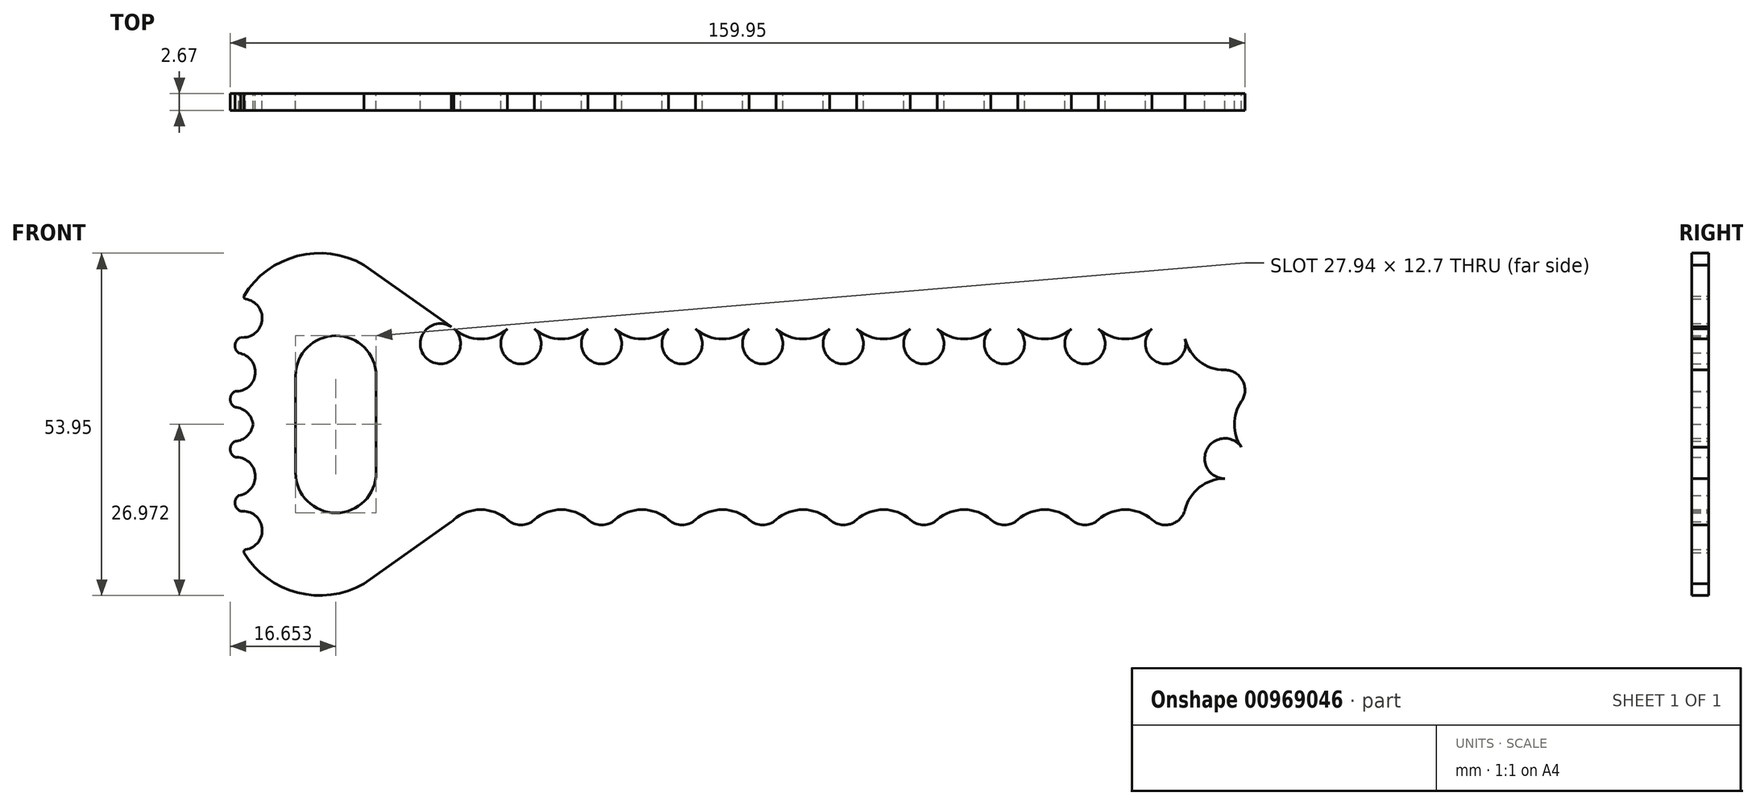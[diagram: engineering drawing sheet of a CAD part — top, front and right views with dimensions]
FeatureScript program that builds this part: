
annotation { "Feature Type Name" : "Feature", "Feature Type Description" : "" }
export const myFeature = defineFeature(function(context is Context, id is Id, definition is map)
    precondition{}
    {
        {
            var Q0;
            Q0=qCreatedBy(makeId("Front.planeOp"),FACE);
            var sketch = newSketch(context, id + "F0", { "sketchPlane" : qUnion([Q0])});
            skLineSegment(sketch, "E0.right", {"start": v(61.78, -7.38) * mm, "end": v(61.78, -7.89) * mm, "construction": true});
            skCircle(sketch, "E1.MirrorC", {"center": v(-65.29, -1.2) * mm, "radius": 3.18 * mm});
            skCircle(sketch, "E2", {"center": v(58.36, -8.5) * mm, "radius": 3.18 * mm});
            skArc(sketch, "E3.MirrorCS", {"start": v(-54.7, 1.16) * mm, "mid": v(-58.94, -0.46) * mm, "end": v(-63.17, 1.16) * mm});
            skCircle(sketch, "E4.MirrorC", {"center": v(-52.59, -1.2) * mm, "radius": 3.18 * mm});
            skCircle(sketch, "E5.MirrorC", {"center": v(-39.89, -1.2) * mm, "radius": 3.18 * mm});
            skCircle(sketch, "E6.MirrorC", {"center": v(-27.19, -1.2) * mm, "radius": 3.18 * mm});
            skCircle(sketch, "E7.MirrorC", {"center": v(-14.49, -1.2) * mm, "radius": 3.18 * mm});
            skCircle(sketch, "E8.MirrorC", {"center": v(-1.79, -1.2) * mm, "radius": 3.18 * mm});
            skCircle(sketch, "E9.MirrorC", {"center": v(10.91, -1.2) * mm, "radius": 3.18 * mm});
            skCircle(sketch, "E10.MirrorC", {"center": v(23.61, -1.2) * mm, "radius": 3.18 * mm});
            skCircle(sketch, "E11.MirrorC", {"center": v(36.31, -1.2) * mm, "radius": 3.18 * mm});
            skCircle(sketch, "E12.MirrorC", {"center": v(49.01, -1.2) * mm, "radius": 3.18 * mm});
            skArc(sketch, "E13.MirrorCS", {"start": v(-42, 1.16) * mm, "mid": v(-46.24, -0.46) * mm, "end": v(-50.47, 1.16) * mm});
            skArc(sketch, "E14.MirrorCS", {"start": v(-29.3, 1.16) * mm, "mid": v(-33.54, -0.46) * mm, "end": v(-37.77, 1.16) * mm});
            skArc(sketch, "E15.MirrorCS", {"start": v(-16.6, 1.16) * mm, "mid": v(-20.84, -0.46) * mm, "end": v(-25.07, 1.16) * mm});
            skArc(sketch, "E16.MirrorCS", {"start": v(-3.9, 1.16) * mm, "mid": v(-8.14, -0.46) * mm, "end": v(-12.37, 1.16) * mm});
            skArc(sketch, "E17.MirrorCS", {"start": v(8.8, 1.16) * mm, "mid": v(4.56, -0.46) * mm, "end": v(0.33, 1.16) * mm});
            skArc(sketch, "E18.MirrorCS", {"start": v(21.5, 1.16) * mm, "mid": v(17.26, -0.46) * mm, "end": v(13.03, 1.16) * mm});
            skArc(sketch, "E19.MirrorCS", {"start": v(34.2, 1.16) * mm, "mid": v(29.96, -0.46) * mm, "end": v(25.73, 1.16) * mm});
            skArc(sketch, "E20.MirrorCS", {"start": v(46.9, 1.16) * mm, "mid": v(42.66, -0.46) * mm, "end": v(38.43, 1.16) * mm});
            skArc(sketch, "E21", {"start": v(52.1, -0.47) * mm, "mid": v(54.36, -3.99) * mm, "end": v(58.33, -5.33) * mm});
            skArc(sketch, "E22", {"start": v(60.97, -10.3) * mm, "mid": v(60.14, -12.02) * mm, "end": v(59.86, -13.9) * mm});
            skPoint(sketch, "E23.middle", {"position": v(-75.42, -13.9) * mm});
            skArc(sketch, "E24", {"start": v(-62.11, -13.9) * mm, "mid": v(-65.29, -10.73) * mm, "end": v(-68.46, -13.9) * mm, "construction": true});
            skPoint(sketch, "E25.center", {"position": v(0.47, -13.9) * mm});
            skPoint(sketch, "E26.visualSharp", {"position": v(-88.5, 10.24) * mm});
            skArc(sketch, "E27.MirrorCS", {"start": v(-42, -3.57) * mm, "mid": v(-46.24, -1.96) * mm, "end": v(-50.47, -3.57) * mm, "construction": true});
            skArc(sketch, "E28.MirrorCS", {"start": v(-29.3, -3.57) * mm, "mid": v(-33.54, -1.96) * mm, "end": v(-37.77, -3.57) * mm, "construction": true});
            skArc(sketch, "E29.MirrorCS", {"start": v(-16.6, -3.57) * mm, "mid": v(-20.84, -1.96) * mm, "end": v(-25.07, -3.57) * mm, "construction": true});
            skArc(sketch, "E30.MirrorCS", {"start": v(-3.9, -3.57) * mm, "mid": v(-8.14, -1.96) * mm, "end": v(-12.37, -3.57) * mm, "construction": true});
            skArc(sketch, "E31.MirrorCS", {"start": v(8.8, -3.57) * mm, "mid": v(4.56, -1.96) * mm, "end": v(0.33, -3.57) * mm, "construction": true});
            skArc(sketch, "E32.MirrorCS", {"start": v(21.5, -3.57) * mm, "mid": v(17.26, -1.96) * mm, "end": v(13.03, -3.57) * mm, "construction": true});
            skArc(sketch, "E33.MirrorCS", {"start": v(34.2, -3.57) * mm, "mid": v(29.96, -1.96) * mm, "end": v(25.73, -3.57) * mm, "construction": true});
            skArc(sketch, "E34.MirrorCS", {"start": v(46.9, -3.57) * mm, "mid": v(42.66, -1.96) * mm, "end": v(38.43, -3.57) * mm, "construction": true});
            skArc(sketch, "E35", {"start": v(55.27, -9.25) * mm, "mid": v(53, -5.73) * mm, "end": v(49.04, -4.38) * mm, "construction": true});
            skArc(sketch, "E36", {"start": v(56.86, -13.9) * mm, "mid": v(56.58, -12.02) * mm, "end": v(55.74, -10.3) * mm, "construction": true});
            skCircle(sketch, "E37", {"center": v(-65.29, -1.2) * mm, "radius": 0.8 * mm, "construction": true});
            skArc(sketch, "E38", {"start": v(-64.49, -13.9) * mm, "mid": v(-65.29, -13.1) * mm, "end": v(-66.09, -13.9) * mm, "construction": true});
            skCircle(sketch, "E39", {"center": v(-52.59, -1.2) * mm, "radius": 0.8 * mm, "construction": true});
            skCircle(sketch, "E40", {"center": v(-39.89, -1.2) * mm, "radius": 0.8 * mm, "construction": true});
            skCircle(sketch, "E41", {"center": v(-27.19, -1.2) * mm, "radius": 0.8 * mm, "construction": true});
            skCircle(sketch, "E42", {"center": v(-14.49, -1.2) * mm, "radius": 0.8 * mm, "construction": true});
            skCircle(sketch, "E43", {"center": v(-1.79, -1.2) * mm, "radius": 0.8 * mm, "construction": true});
            skCircle(sketch, "E44", {"center": v(10.91, -1.2) * mm, "radius": 0.8 * mm, "construction": true});
            skCircle(sketch, "E45", {"center": v(23.61, -1.2) * mm, "radius": 0.8 * mm, "construction": true});
            skCircle(sketch, "E46", {"center": v(36.31, -1.2) * mm, "radius": 0.8 * mm, "construction": true});
            skCircle(sketch, "E47", {"center": v(49.01, -1.2) * mm, "radius": 0.8 * mm, "construction": true});
            skCircle(sketch, "E48", {"center": v(58.36, -8.5) * mm, "radius": 0.8 * mm, "construction": true});
            skArc(sketch, "E49", {"start": v(-54.7, -3.57) * mm, "mid": v(-58.94, -1.96) * mm, "end": v(-63.17, -3.57) * mm, "construction": true});
            skArc(sketch, "E50", {"start": v(-68.3, -12.92) * mm, "mid": v(-67.45, -7.56) * mm, "end": v(-68.3, -2.2) * mm, "construction": true});
            skArc(sketch, "E51", {"start": v(-63.4, -3.76) * mm, "mid": v(-63.9, -8.12) * mm, "end": v(-62.55, -12.3) * mm, "construction": true});
            skPoint(sketch, "E52.visualSharp", {"position": v(-96, 7.56) * mm});
            skArc(sketch, "E53", {"start": v(-96.74, -0.2) * mm, "mid": v(-93.4, 2.44) * mm, "end": v(-95.98, 5.82) * mm});
            skArc(sketch, "E54.2.0", {"start": v(48.77, 84.47) * mm, "mid": v(48.66, 79.8) * mm, "end": v(53.28, 80.57) * mm});
            skPoint(sketch, "E54.center", {"position": v(0, 0) * mm});
            skArc(sketch, "E55.1.0", {"start": v(-97.65, -8.72) * mm, "mid": v(-94.48, -5.99) * mm, "end": v(-97.06, -2.68) * mm});
            skArc(sketch, "E55.2.0", {"start": v(-94.83, -13.9) * mm, "mid": v(-95.76, -12.06) * mm, "end": v(-97.65, -11.23) * mm});
            skArc(sketch, "E56", {"start": v(-96.74, -0.2) * mm, "mid": v(-97.65, -1.34) * mm, "end": v(-97.06, -2.68) * mm});
            skArc(sketch, "E57", {"start": v(-97.65, -8.72) * mm, "mid": v(-98.42, -9.97) * mm, "end": v(-97.65, -11.23) * mm});
            skPoint(sketch, "E57.startSnap0", {"position": v(-97.65, -1.33) * mm});
            skPoint(sketch, "E57.endSnap0", {"position": v(-97.65, -1.33) * mm});
            skPoint(sketch, "E58.orphan", {"position": v(-97.77, -2.66) * mm});
            skArc(sketch, "E59", {"start": v(-96.27, 6.3) * mm, "mid": v(-96.23, 6) * mm, "end": v(-95.98, 5.82) * mm});
            skPoint(sketch, "E60.orphan", {"position": v(-96.41, 5.86) * mm});
            skPoint(sketch, "E61.orphan", {"position": v(-98.38, -8.6) * mm});
            skPoint(sketch, "E62.orphan", {"position": v(-98.37, -11.27) * mm});
            skArc(sketch, "E63.MirrorCS", {"start": v(-96.27, -34.12) * mm, "mid": v(-96.23, -33.82) * mm, "end": v(-95.98, -33.64) * mm});
            skCircle(sketch, "E64.MirrorC", {"center": v(-52.59, -26.6) * mm, "radius": 0.8 * mm, "construction": true});
            skCircle(sketch, "E65.MirrorC", {"center": v(-14.49, -26.6) * mm, "radius": 0.8 * mm, "construction": true});
            skCircle(sketch, "E66.MirrorC", {"center": v(23.61, -26.6) * mm, "radius": 0.8 * mm, "construction": true});
            skArc(sketch, "E67.MirrorCS", {"start": v(-96.74, -27.62) * mm, "mid": v(-97.65, -26.47) * mm, "end": v(-97.06, -25.13) * mm});
            skCircle(sketch, "E68.MirrorC", {"center": v(-65.29, -26.6) * mm, "radius": 0.8 * mm, "construction": true});
            skCircle(sketch, "E69.MirrorC", {"center": v(-27.19, -26.6) * mm, "radius": 0.8 * mm, "construction": true});
            skCircle(sketch, "E70.MirrorC", {"center": v(36.31, -26.6) * mm, "radius": 0.8 * mm, "construction": true});
            skCircle(sketch, "E71.MirrorC", {"center": v(-1.79, -26.6) * mm, "radius": 0.8 * mm, "construction": true});
            skCircle(sketch, "E72.MirrorC", {"center": v(10.91, -26.6) * mm, "radius": 0.8 * mm, "construction": true});
            skCircle(sketch, "E73.MirrorC", {"center": v(49.01, -26.6) * mm, "radius": 0.8 * mm, "construction": true});
            skCircle(sketch, "E74.MirrorC", {"center": v(-39.89, -26.6) * mm, "radius": 0.8 * mm, "construction": true});
            skPoint(sketch, "E75.MirrorP", {"position": v(-97.65, -26.48) * mm});
            skCircle(sketch, "E76.MirrorC", {"center": v(-27.19, -26.6) * mm, "radius": 3.18 * mm});
            skCircle(sketch, "E77.MirrorC", {"center": v(-65.29, -26.6) * mm, "radius": 3.18 * mm});
            skCircle(sketch, "E78.MirrorC", {"center": v(-52.59, -26.6) * mm, "radius": 3.18 * mm});
            skArc(sketch, "E79.MirrorCS", {"start": v(34.2, -28.97) * mm, "mid": v(29.96, -27.36) * mm, "end": v(25.73, -28.97) * mm});
            skArc(sketch, "E80.MirrorCS", {"start": v(21.5, -28.97) * mm, "mid": v(17.26, -27.36) * mm, "end": v(13.03, -28.97) * mm});
            skArc(sketch, "E81.MirrorCS", {"start": v(46.9, -24.24) * mm, "mid": v(42.66, -25.86) * mm, "end": v(38.43, -24.24) * mm, "construction": true});
            skArc(sketch, "E82.MirrorCS", {"start": v(46.9, -28.97) * mm, "mid": v(42.66, -27.36) * mm, "end": v(38.43, -28.97) * mm});
            skPoint(sketch, "E83.MirrorP", {"position": v(-97.77, -25.15) * mm});
            skArc(sketch, "E84.MirrorCS", {"start": v(-54.7, -28.97) * mm, "mid": v(-58.94, -27.36) * mm, "end": v(-63.17, -28.97) * mm});
            skCircle(sketch, "E85.MirrorC", {"center": v(-14.49, -26.6) * mm, "radius": 3.18 * mm});
            skArc(sketch, "E86.MirrorCS", {"start": v(34.2, -24.24) * mm, "mid": v(29.96, -25.86) * mm, "end": v(25.73, -24.24) * mm, "construction": true});
            skPoint(sketch, "E87.MirrorP", {"position": v(0, -27.82) * mm});
            skArc(sketch, "E88.MirrorCS", {"start": v(8.8, -28.97) * mm, "mid": v(4.56, -27.36) * mm, "end": v(0.33, -28.97) * mm});
            skArc(sketch, "E89.MirrorCS", {"start": v(-63.4, -24.06) * mm, "mid": v(-63.9, -19.7) * mm, "end": v(-62.55, -15.5) * mm, "construction": true});
            skArc(sketch, "E90.MirrorCS", {"start": v(-97.65, -19.1) * mm, "mid": v(-94.48, -21.83) * mm, "end": v(-97.06, -25.13) * mm});
            skArc(sketch, "E91.MirrorCS", {"start": v(-96.74, -27.62) * mm, "mid": v(-93.4, -30.26) * mm, "end": v(-95.98, -33.64) * mm});
            skCircle(sketch, "E92.MirrorC", {"center": v(23.61, -26.6) * mm, "radius": 3.18 * mm});
            skArc(sketch, "E93.MirrorCS", {"start": v(-42, -24.24) * mm, "mid": v(-46.24, -25.86) * mm, "end": v(-50.47, -24.24) * mm, "construction": true});
            skArc(sketch, "E94.MirrorCS", {"start": v(-42, -28.97) * mm, "mid": v(-46.24, -27.36) * mm, "end": v(-50.47, -28.97) * mm});
            skPoint(sketch, "E95.MirrorP", {"position": v(-96.41, -33.67) * mm});
            skCircle(sketch, "E96.MirrorC", {"center": v(36.31, -26.6) * mm, "radius": 3.18 * mm});
            skArc(sketch, "E97.MirrorCS", {"start": v(-3.9, -24.24) * mm, "mid": v(-8.14, -25.86) * mm, "end": v(-12.37, -24.24) * mm, "construction": true});
            skCircle(sketch, "E98.MirrorC", {"center": v(10.91, -26.6) * mm, "radius": 3.18 * mm});
            skArc(sketch, "E99.MirrorCS", {"start": v(21.5, -24.24) * mm, "mid": v(17.26, -25.86) * mm, "end": v(13.03, -24.24) * mm, "construction": true});
            skArc(sketch, "E100.MirrorCS", {"start": v(-68.3, -14.9) * mm, "mid": v(-67.45, -20.26) * mm, "end": v(-68.3, -25.62) * mm, "construction": true});
            skArc(sketch, "E101.MirrorCS", {"start": v(8.8, -24.24) * mm, "mid": v(4.56, -25.86) * mm, "end": v(0.33, -24.24) * mm, "construction": true});
            skArc(sketch, "E102.MirrorCS", {"start": v(55.27, -18.57) * mm, "mid": v(53, -22.09) * mm, "end": v(49.04, -23.43) * mm, "construction": true});
            skCircle(sketch, "E103.MirrorC", {"center": v(-1.79, -26.6) * mm, "radius": 3.18 * mm});
            skArc(sketch, "E104.MirrorCS", {"start": v(-16.6, -24.24) * mm, "mid": v(-20.84, -25.86) * mm, "end": v(-25.07, -24.24) * mm, "construction": true});
            skArc(sketch, "E105.MirrorCS", {"start": v(-54.7, -24.24) * mm, "mid": v(-58.94, -25.86) * mm, "end": v(-63.17, -24.24) * mm, "construction": true});
            skCircle(sketch, "E106.MirrorC", {"center": v(49.01, -26.6) * mm, "radius": 3.18 * mm});
            skArc(sketch, "E107.MirrorCS", {"start": v(-29.3, -28.97) * mm, "mid": v(-33.54, -27.36) * mm, "end": v(-37.77, -28.97) * mm});
            skArc(sketch, "E108.MirrorCS", {"start": v(-16.6, -28.97) * mm, "mid": v(-20.84, -27.36) * mm, "end": v(-25.07, -28.97) * mm});
            skCircle(sketch, "E109.MirrorC", {"center": v(58.36, -19.3) * mm, "radius": 3.18 * mm});
            skArc(sketch, "E110.MirrorCS", {"start": v(52.1, -27.35) * mm, "mid": v(54.36, -23.83) * mm, "end": v(58.33, -22.48) * mm});
            skArc(sketch, "E111.MirrorCS", {"start": v(-29.3, -24.24) * mm, "mid": v(-33.54, -25.86) * mm, "end": v(-37.77, -24.24) * mm, "construction": true});
            skCircle(sketch, "E112.MirrorC", {"center": v(-39.89, -26.6) * mm, "radius": 3.18 * mm});
            skArc(sketch, "E113.MirrorCS", {"start": v(-3.9, -28.97) * mm, "mid": v(-8.14, -27.36) * mm, "end": v(-12.37, -28.97) * mm});
            skArc(sketch, "E114.MirrorCS", {"start": v(-94.83, -13.9) * mm, "mid": v(-95.76, -15.76) * mm, "end": v(-97.65, -16.59) * mm});
            skArc(sketch, "E115.MirrorCS", {"start": v(-97.65, -19.1) * mm, "mid": v(-98.42, -17.84) * mm, "end": v(-97.65, -16.59) * mm});
            skArc(sketch, "E116.MirrorCS", {"start": v(-62.11, -13.9) * mm, "mid": v(-65.29, -17.08) * mm, "end": v(-68.46, -13.9) * mm, "construction": true});
            skArc(sketch, "E117.MirrorCS", {"start": v(-64.49, -13.9) * mm, "mid": v(-65.29, -14.7) * mm, "end": v(-66.09, -13.9) * mm, "construction": true});
            skArc(sketch, "E118.MirrorCS", {"start": v(56.86, -13.9) * mm, "mid": v(56.58, -15.8) * mm, "end": v(55.74, -17.5) * mm, "construction": true});
            skArc(sketch, "E119.MirrorCS", {"start": v(60.97, -17.5) * mm, "mid": v(60.14, -15.8) * mm, "end": v(59.86, -13.9) * mm});
            skCircle(sketch, "E120.MirrorC", {"center": v(58.36, -19.3) * mm, "radius": 0.8 * mm, "construction": true});
            skPoint(sketch, "E121.end.orphan", {"position": v(-64.78, 1.93) * mm});
            skPoint(sketch, "E122.MirrorCS.end.orphan", {"position": v(-64.78, -29.74) * mm});
            skLineSegment(sketch, "E123", {"start": v(-63.58, 1.47) * mm, "end": v(-77.34, 11.21) * mm});
            skPoint(sketch, "E26.filletArc.end.orphan", {"position": v(-88.03, 11.03) * mm});
            skLineSegment(sketch, "E124.bottom", {"start": v(-75.42, -13.9) * mm, "end": v(-88.12, -13.9) * mm});
            skLineSegment(sketch, "E124.left", {"start": v(-75.42, -13.9) * mm, "end": v(-75.42, -6.28) * mm});
            skLineSegment(sketch, "E124.right", {"start": v(-88.12, -13.9) * mm, "end": v(-88.12, -6.28) * mm});
            skPoint(sketch, "E125.endSnap0", {"position": v(-75.42, -6.95) * mm});
            skArc(sketch, "E126", {"start": v(-75.42, -6.3) * mm, "mid": v(-81.77, 0.06) * mm, "end": v(-88.12, -6.3) * mm});
            skPoint(sketch, "E127.orphan", {"position": v(-88.12, 0) * mm});
            skPoint(sketch, "E128.orphan", {"position": v(-75.42, 0) * mm});
            skPoint(sketch, "E52.filletArc.center.orphan", {"position": v(-93.32, 5.15) * mm});
            skPoint(sketch, "E52.filletArc.start.orphan", {"position": v(-94.38, 8.14) * mm});
            skArc(sketch, "E129", {"start": v(-77.34, 11.21) * mm, "mid": v(-87.8, 12.62) * mm, "end": v(-96.27, 6.3) * mm});
            skLineSegment(sketch, "E130.MirrorCS", {"start": v(-88.12, -13.9) * mm, "end": v(-88.12, -21.54) * mm});
            skArc(sketch, "E131.MirrorCS", {"start": v(-75.42, -21.52) * mm, "mid": v(-81.77, -27.88) * mm, "end": v(-88.12, -21.52) * mm});
            skLineSegment(sketch, "E132.MirrorCS", {"start": v(-75.42, -13.9) * mm, "end": v(-75.42, -21.54) * mm});
            skLineSegment(sketch, "E133.MirrorCS", {"start": v(-63.58, -29.28) * mm, "end": v(-77.34, -39.03) * mm});
            skArc(sketch, "E134.MirrorCS", {"start": v(-77.34, -39.03) * mm, "mid": v(-87.8, -40.44) * mm, "end": v(-96.27, -34.12) * mm});
            skText(sketch, "E135", { "text": "OTHG", "fontName": "OpenSans-Regular.ttf"});
            const initialGuessF0  = {"E135": [-0.03533, -0.02248, 1, 0, 0.0175]};
            skSetInitialGuess(sketch, initialGuessF0);
            skSolve(sketch);
        }
        {
            var Q0;
            {var subQ25=sQuery(id+"F0.wireOp",EDGE,"E3.MirrorCS");Q0=makeQuery(id+"F0.imprint","IMPRINT",FACE,{"disambiguationData":[TD([[makeQuery(id+"F0.imprint","IMPRINT",EDGE,{"derivedFrom":subQ25}),1.0]])]});}
            var Q1;
            {var subQ0=sQuery(id+"F0.wireOp",EDGE,"E1.MirrorC");var subQ1=makeQuery(id+"F0.imprint","INTERSECT",VERTEX,{"derivedFrom":[subQ0,sQuery(id+"F0.wireOp",EDGE,"E3.MirrorCS")]});Q1=makeQuery(id+"F0.imprint","IMPRINT",FACE,{"disambiguationData":[TD([[makeQuery(id+"F0.imprint","IMPRINT",EDGE,{"disambiguationData":[TD([[subQ1,1.0]])],"derivedFrom":subQ0}),-1.0]])]});}
            var Q2;
            {var subQ0=sQuery(id+"F0.wireOp",EDGE,"E4.MirrorC");var subQ1=makeQuery(id+"F0.imprint","INTERSECT",VERTEX,{"derivedFrom":[sQuery(id+"F0.wireOp",EDGE,"E3.MirrorCS"),subQ0]});Q2=makeQuery(id+"F0.imprint","IMPRINT",FACE,{"disambiguationData":[TD([[makeQuery(id+"F0.imprint","IMPRINT",EDGE,{"disambiguationData":[TD([[subQ1,-1.0]])],"derivedFrom":subQ0}),-1.0]])]});}
            var Q3;
            {var subQ0=sQuery(id+"F0.wireOp",EDGE,"E5.MirrorC");var subQ1=makeQuery(id+"F0.imprint","INTERSECT",VERTEX,{"derivedFrom":[subQ0,sQuery(id+"F0.wireOp",EDGE,"E13.MirrorCS")]});Q3=makeQuery(id+"F0.imprint","IMPRINT",FACE,{"disambiguationData":[TD([[makeQuery(id+"F0.imprint","IMPRINT",EDGE,{"disambiguationData":[TD([[subQ1,-1.0]])],"derivedFrom":subQ0}),-1.0]])]});}
            var Q4;
            {var subQ0=sQuery(id+"F0.wireOp",EDGE,"E6.MirrorC");var subQ1=makeQuery(id+"F0.imprint","INTERSECT",VERTEX,{"derivedFrom":[subQ0,sQuery(id+"F0.wireOp",EDGE,"E14.MirrorCS")]});Q4=makeQuery(id+"F0.imprint","IMPRINT",FACE,{"disambiguationData":[TD([[makeQuery(id+"F0.imprint","IMPRINT",EDGE,{"disambiguationData":[TD([[subQ1,-1.0]])],"derivedFrom":subQ0}),-1.0]])]});}
            var Q5;
            {var subQ0=sQuery(id+"F0.wireOp",EDGE,"E7.MirrorC");var subQ1=makeQuery(id+"F0.imprint","INTERSECT",VERTEX,{"derivedFrom":[subQ0,sQuery(id+"F0.wireOp",EDGE,"E15.MirrorCS")]});Q5=makeQuery(id+"F0.imprint","IMPRINT",FACE,{"disambiguationData":[TD([[makeQuery(id+"F0.imprint","IMPRINT",EDGE,{"disambiguationData":[TD([[subQ1,-1.0]])],"derivedFrom":subQ0}),-1.0]])]});}
            var Q6;
            {var subQ0=sQuery(id+"F0.wireOp",EDGE,"E8.MirrorC");var subQ1=makeQuery(id+"F0.imprint","INTERSECT",VERTEX,{"derivedFrom":[subQ0,sQuery(id+"F0.wireOp",EDGE,"E16.MirrorCS")]});Q6=makeQuery(id+"F0.imprint","IMPRINT",FACE,{"disambiguationData":[TD([[makeQuery(id+"F0.imprint","IMPRINT",EDGE,{"disambiguationData":[TD([[subQ1,-1.0]])],"derivedFrom":subQ0}),-1.0]])]});}
            var Q7;
            {var subQ0=sQuery(id+"F0.wireOp",EDGE,"E9.MirrorC");var subQ1=makeQuery(id+"F0.imprint","INTERSECT",VERTEX,{"derivedFrom":[subQ0,sQuery(id+"F0.wireOp",EDGE,"E17.MirrorCS")]});Q7=makeQuery(id+"F0.imprint","IMPRINT",FACE,{"disambiguationData":[TD([[makeQuery(id+"F0.imprint","IMPRINT",EDGE,{"disambiguationData":[TD([[subQ1,-1.0]])],"derivedFrom":subQ0}),-1.0]])]});}
            var Q8;
            {var subQ0=sQuery(id+"F0.wireOp",EDGE,"E10.MirrorC");var subQ1=makeQuery(id+"F0.imprint","INTERSECT",VERTEX,{"derivedFrom":[subQ0,sQuery(id+"F0.wireOp",EDGE,"E18.MirrorCS")]});Q8=makeQuery(id+"F0.imprint","IMPRINT",FACE,{"disambiguationData":[TD([[makeQuery(id+"F0.imprint","IMPRINT",EDGE,{"disambiguationData":[TD([[subQ1,-1.0]])],"derivedFrom":subQ0}),-1.0]])]});}
            var Q9;
            {var subQ0=sQuery(id+"F0.wireOp",EDGE,"E11.MirrorC");var subQ1=makeQuery(id+"F0.imprint","INTERSECT",VERTEX,{"derivedFrom":[subQ0,sQuery(id+"F0.wireOp",EDGE,"E19.MirrorCS")]});Q9=makeQuery(id+"F0.imprint","IMPRINT",FACE,{"disambiguationData":[TD([[makeQuery(id+"F0.imprint","IMPRINT",EDGE,{"disambiguationData":[TD([[subQ1,-1.0]])],"derivedFrom":subQ0}),-1.0]])]});}
            var Q10;
            {var subQ0=sQuery(id+"F0.wireOp",EDGE,"E12.MirrorC");var subQ1=makeQuery(id+"F0.imprint","INTERSECT",VERTEX,{"derivedFrom":[subQ0,sQuery(id+"F0.wireOp",EDGE,"E20.MirrorCS")]});Q10=makeQuery(id+"F0.imprint","IMPRINT",FACE,{"disambiguationData":[TD([[makeQuery(id+"F0.imprint","IMPRINT",EDGE,{"disambiguationData":[TD([[subQ1,-1.0]])],"derivedFrom":subQ0}),-1.0]])]});}
            var Q11;
            {var subQ0=sQuery(id+"F0.wireOp",EDGE,"E2");var subQ1=makeQuery(id+"F0.imprint","INTERSECT",VERTEX,{"derivedFrom":[subQ0,sQuery(id+"F0.wireOp",EDGE,"E21")]});Q11=makeQuery(id+"F0.imprint","IMPRINT",FACE,{"disambiguationData":[TD([[makeQuery(id+"F0.imprint","IMPRINT",EDGE,{"disambiguationData":[TD([[subQ1,-1.0]])],"derivedFrom":subQ0}),1.0]])]});}
            var Q12;
            {var subQ0=sQuery(id+"F0.wireOp",EDGE,"E109.MirrorC");var subQ1=makeQuery(id+"F0.imprint","INTERSECT",VERTEX,{"derivedFrom":[subQ0,sQuery(id+"F0.wireOp",EDGE,"E110.MirrorCS")]});Q12=makeQuery(id+"F0.imprint","IMPRINT",FACE,{"disambiguationData":[TD([[makeQuery(id+"F0.imprint","IMPRINT",EDGE,{"disambiguationData":[TD([[subQ1,-1.0]])],"derivedFrom":subQ0}),-1.0]])]});}
            var Q13;
            {var subQ0=sQuery(id+"F0.wireOp",EDGE,"E106.MirrorC");var subQ1=makeQuery(id+"F0.imprint","INTERSECT",VERTEX,{"derivedFrom":[sQuery(id+"F0.wireOp",EDGE,"E82.MirrorCS"),subQ0]});Q13=makeQuery(id+"F0.imprint","IMPRINT",FACE,{"disambiguationData":[TD([[makeQuery(id+"F0.imprint","IMPRINT",EDGE,{"disambiguationData":[TD([[subQ1,-1.0]])],"derivedFrom":subQ0}),1.0]])]});}
            var Q14;
            {var subQ0=sQuery(id+"F0.wireOp",EDGE,"E96.MirrorC");var subQ1=makeQuery(id+"F0.imprint","INTERSECT",VERTEX,{"derivedFrom":[sQuery(id+"F0.wireOp",EDGE,"E79.MirrorCS"),subQ0]});Q14=makeQuery(id+"F0.imprint","IMPRINT",FACE,{"disambiguationData":[TD([[makeQuery(id+"F0.imprint","IMPRINT",EDGE,{"disambiguationData":[TD([[subQ1,-1.0]])],"derivedFrom":subQ0}),1.0]])]});}
            var Q15;
            {var subQ0=sQuery(id+"F0.wireOp",EDGE,"E92.MirrorC");var subQ1=makeQuery(id+"F0.imprint","INTERSECT",VERTEX,{"derivedFrom":[sQuery(id+"F0.wireOp",EDGE,"E79.MirrorCS"),subQ0]});Q15=makeQuery(id+"F0.imprint","IMPRINT",FACE,{"disambiguationData":[TD([[makeQuery(id+"F0.imprint","IMPRINT",EDGE,{"disambiguationData":[TD([[subQ1,1.0]])],"derivedFrom":subQ0}),1.0]])]});}
            var Q16;
            {var subQ0=sQuery(id+"F0.wireOp",EDGE,"E98.MirrorC");var subQ1=makeQuery(id+"F0.imprint","INTERSECT",VERTEX,{"derivedFrom":[sQuery(id+"F0.wireOp",EDGE,"E80.MirrorCS"),subQ0]});Q16=makeQuery(id+"F0.imprint","IMPRINT",FACE,{"disambiguationData":[TD([[makeQuery(id+"F0.imprint","IMPRINT",EDGE,{"disambiguationData":[TD([[subQ1,1.0]])],"derivedFrom":subQ0}),1.0]])]});}
            var Q17;
            {var subQ0=sQuery(id+"F0.wireOp",EDGE,"E103.MirrorC");var subQ1=makeQuery(id+"F0.imprint","INTERSECT",VERTEX,{"derivedFrom":[sQuery(id+"F0.wireOp",EDGE,"E88.MirrorCS"),subQ0]});Q17=makeQuery(id+"F0.imprint","IMPRINT",FACE,{"disambiguationData":[TD([[makeQuery(id+"F0.imprint","IMPRINT",EDGE,{"disambiguationData":[TD([[subQ1,1.0]])],"derivedFrom":subQ0}),1.0]])]});}
            var Q18;
            {var subQ0=sQuery(id+"F0.wireOp",EDGE,"E85.MirrorC");var subQ1=makeQuery(id+"F0.imprint","INTERSECT",VERTEX,{"derivedFrom":[subQ0,sQuery(id+"F0.wireOp",EDGE,"E108.MirrorCS")]});Q18=makeQuery(id+"F0.imprint","IMPRINT",FACE,{"disambiguationData":[TD([[makeQuery(id+"F0.imprint","IMPRINT",EDGE,{"disambiguationData":[TD([[subQ1,-1.0]])],"derivedFrom":subQ0}),1.0]])]});}
            var Q19;
            {var subQ0=sQuery(id+"F0.wireOp",EDGE,"E76.MirrorC");var subQ1=makeQuery(id+"F0.imprint","INTERSECT",VERTEX,{"derivedFrom":[subQ0,sQuery(id+"F0.wireOp",EDGE,"E107.MirrorCS")]});Q19=makeQuery(id+"F0.imprint","IMPRINT",FACE,{"disambiguationData":[TD([[makeQuery(id+"F0.imprint","IMPRINT",EDGE,{"disambiguationData":[TD([[subQ1,-1.0]])],"derivedFrom":subQ0}),1.0]])]});}
            var Q20;
            {var subQ0=sQuery(id+"F0.wireOp",EDGE,"E112.MirrorC");var subQ1=makeQuery(id+"F0.imprint","INTERSECT",VERTEX,{"derivedFrom":[sQuery(id+"F0.wireOp",EDGE,"E94.MirrorCS"),subQ0]});Q20=makeQuery(id+"F0.imprint","IMPRINT",FACE,{"disambiguationData":[TD([[makeQuery(id+"F0.imprint","IMPRINT",EDGE,{"disambiguationData":[TD([[subQ1,-1.0]])],"derivedFrom":subQ0}),1.0]])]});}
            var Q21;
            {var subQ0=sQuery(id+"F0.wireOp",EDGE,"E78.MirrorC");var subQ1=makeQuery(id+"F0.imprint","INTERSECT",VERTEX,{"derivedFrom":[subQ0,sQuery(id+"F0.wireOp",EDGE,"E84.MirrorCS")]});Q21=makeQuery(id+"F0.imprint","IMPRINT",FACE,{"disambiguationData":[TD([[makeQuery(id+"F0.imprint","IMPRINT",EDGE,{"disambiguationData":[TD([[subQ1,-1.0]])],"derivedFrom":subQ0}),1.0]])]});}
            var Q22;
            {var subQ0=sQuery(id+"F0.wireOp",EDGE,"E77.MirrorC");var subQ1=makeQuery(id+"F0.imprint","INTERSECT",VERTEX,{"derivedFrom":[subQ0,sQuery(id+"F0.wireOp",EDGE,"E84.MirrorCS")]});Q22=makeQuery(id+"F0.imprint","IMPRINT",FACE,{"disambiguationData":[TD([[makeQuery(id+"F0.imprint","IMPRINT",EDGE,{"disambiguationData":[TD([[subQ1,1.0]])],"derivedFrom":subQ0}),1.0]])]});}
            var Q23;
            Q23=makeQuery(id+"F0.imprint","IMPRINT",FACE,{"disambiguationData":[TD([[makeQuery(id+"F0.imprint","IMPRINT",EDGE,{"derivedFrom":sQuery(id+"F0.wireOp",EDGE,"E135.sketch_text.stroke-0")}),-1.0]])]});
            var Q24;
            Q24=makeQuery(id+"F0.imprint","IMPRINT",FACE,{"disambiguationData":[TD([[makeQuery(id+"F0.imprint","IMPRINT",EDGE,{"derivedFrom":sQuery(id+"F0.wireOp",EDGE,"E135.sketch_text.stroke-8")}),1.0]])]});
            var Q25;
            Q25=makeQuery(id+"F0.imprint","IMPRINT",FACE,{"disambiguationData":[TD([[makeQuery(id+"F0.imprint","IMPRINT",EDGE,{"derivedFrom":sQuery(id+"F0.wireOp",EDGE,"E135.sketch_text.stroke-24")}),-1.0]])]});
            var Q26;
            Q26=makeQuery(id+"F0.imprint","IMPRINT",FACE,{"disambiguationData":[TD([[makeQuery(id+"F0.imprint","IMPRINT",EDGE,{"derivedFrom":sQuery(id+"F0.wireOp",EDGE,"E135.sketch_text.stroke-16")}),-1.0]])]});
            var Q27;
            Q27=makeQuery(id+"F0.imprint","IMPRINT",FACE,{"disambiguationData":[TD([[makeQuery(id+"F0.imprint","IMPRINT",EDGE,{"derivedFrom":sQuery(id+"F0.wireOp",EDGE,"E135.sketch_text.stroke-36")}),-1.0]])]});
            extrude(context, id + "F1", {"entities" : qUnion([Q0, Q1, Q2, Q3, Q4, Q5, Q6, Q7, Q8, Q9, Q10, Q11, Q12, Q13, Q14, Q15, Q16, Q17, Q18, Q19, Q20, Q21, Q22, Q23, Q24, Q25, Q26, Q27]), "depth" : 2.67 * mm, "offsetDistance" : 25.4 * mm});
        }
    });
